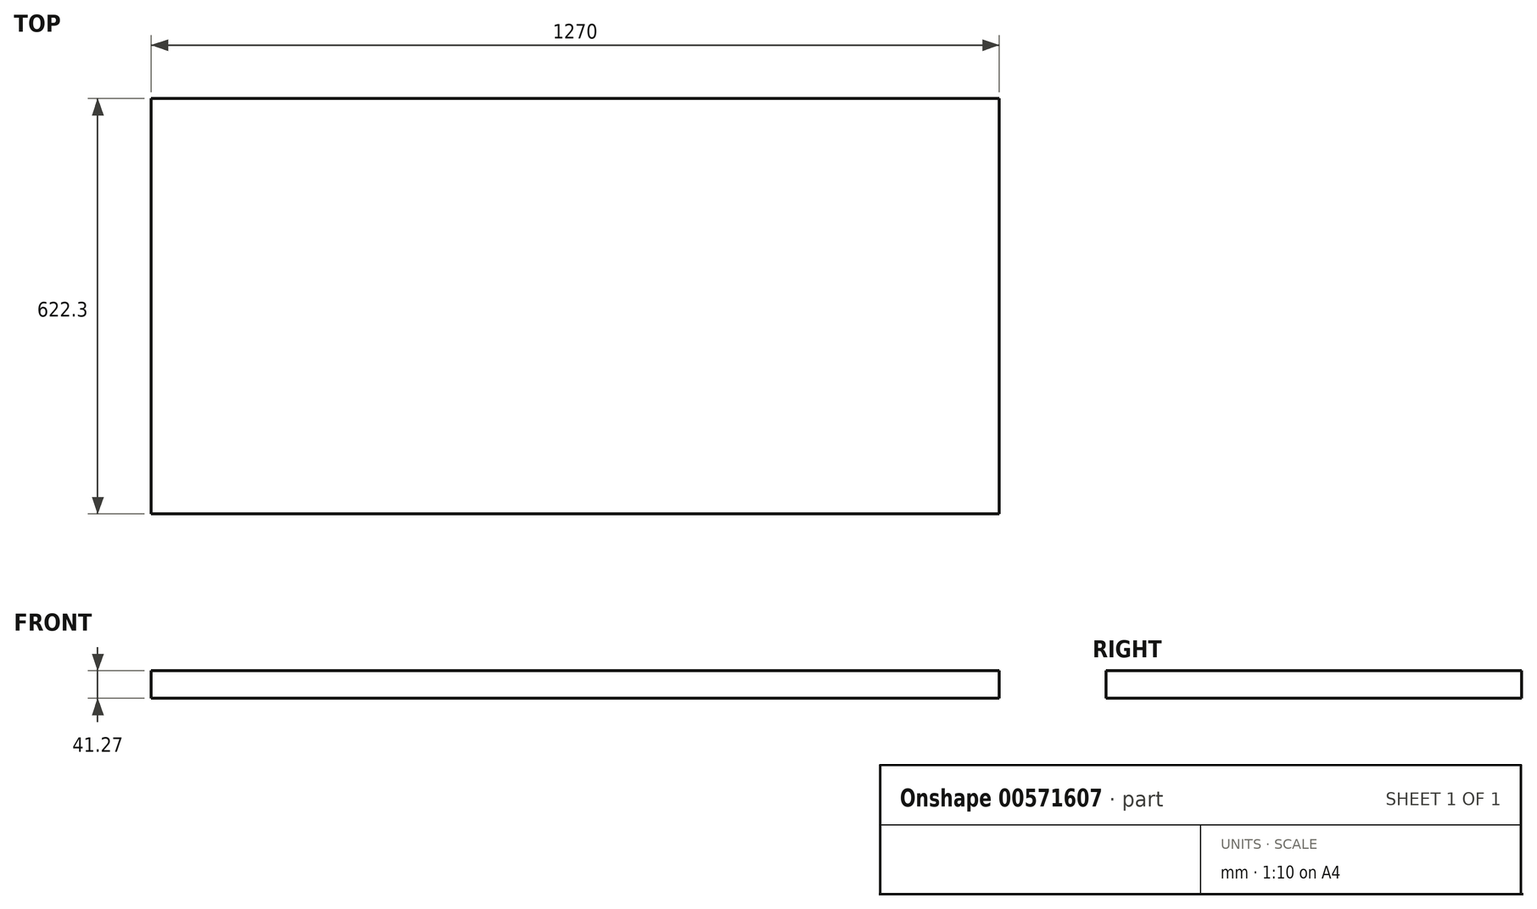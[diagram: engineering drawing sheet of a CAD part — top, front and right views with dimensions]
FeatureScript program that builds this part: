
annotation { "Feature Type Name" : "Feature", "Feature Type Description" : "" }
export const myFeature = defineFeature(function(context is Context, id is Id, definition is map)
    precondition{}
    {
        {
            var Q0;
            Q0=qCreatedBy(makeId("Top.planeOp"),FACE);
            var sketch = newSketch(context, id + "F0", { "sketchPlane" : qUnion([Q0])});
            skLineSegment(sketch, "E0.bottom", {"start": v(0, 0) * mm, "end": v(1270, 0) * mm});
            skLineSegment(sketch, "E0.top", {"start": v(0, 622.3) * mm, "end": v(1270, 622.3) * mm});
            skLineSegment(sketch, "E0.left", {"start": v(0, 0) * mm, "end": v(0, 622.3) * mm});
            skLineSegment(sketch, "E0.right", {"start": v(1270, 0) * mm, "end": v(1270, 622.3) * mm});
            skSolve(sketch);
        }
        {
            var Q0;
            Q0=makeQuery(id+"F0.imprint","IMPRINT",FACE,{"disambiguationData":[TD([[makeQuery(id+"F0.imprint","IMPRINT",EDGE,{"derivedFrom":sQuery(id+"F0.wireOp",EDGE,"E0.bottom")}),1.0]])]});
            extrude(context, id + "F1", {"entities" : qUnion([Q0]), "depth" : 41.27 * mm, "offsetDistance" : 25.4 * mm});
        }
    });
